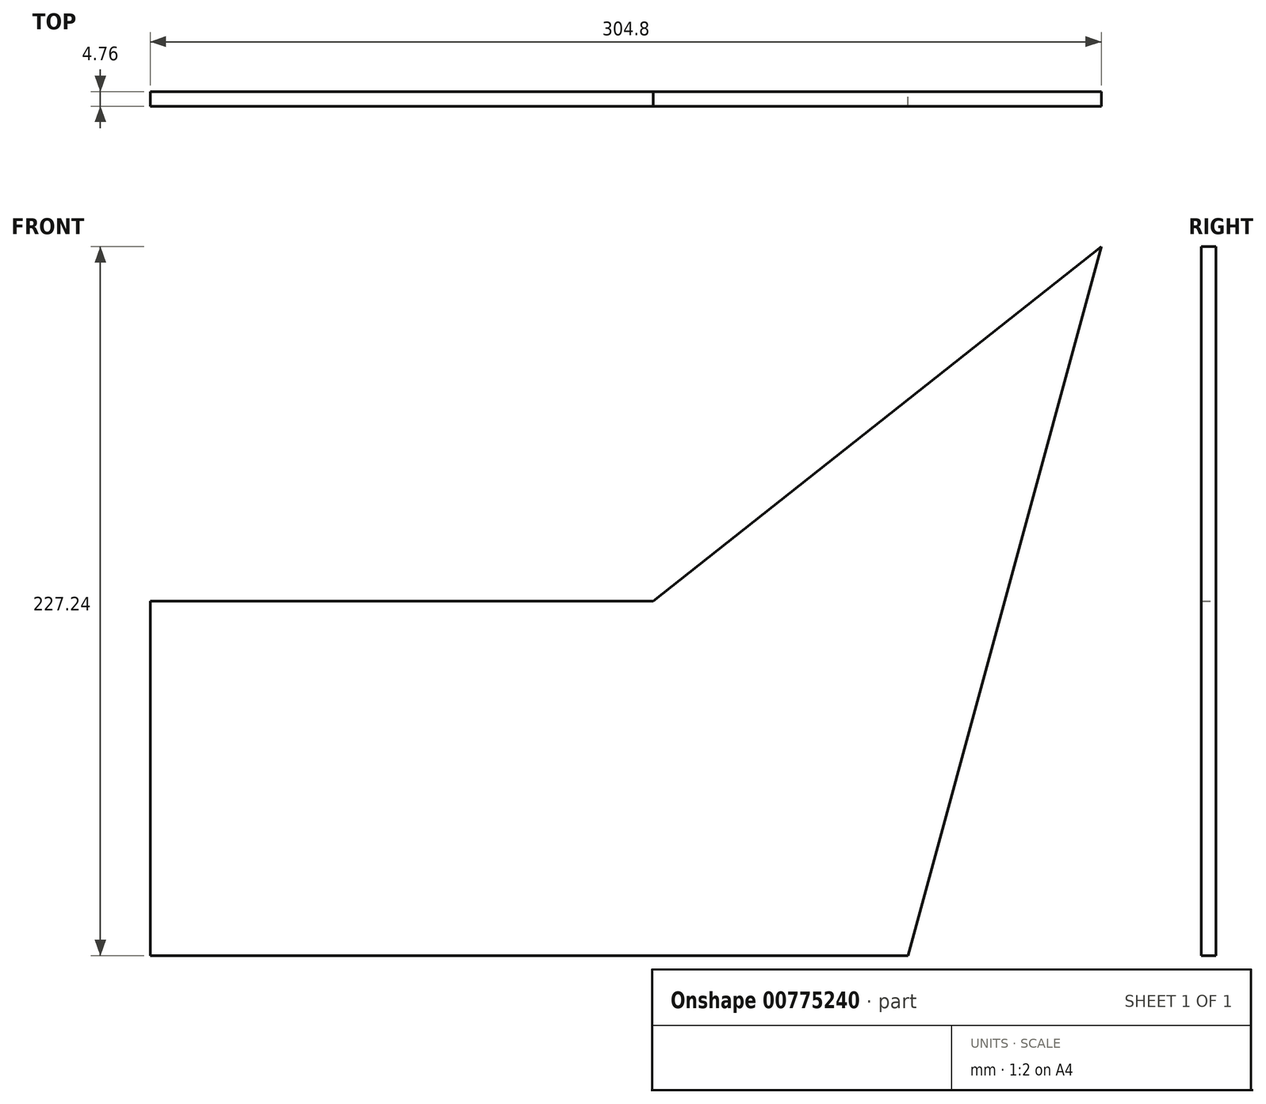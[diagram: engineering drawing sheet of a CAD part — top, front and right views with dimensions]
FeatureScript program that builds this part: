
annotation { "Feature Type Name" : "Feature", "Feature Type Description" : "" }
export const myFeature = defineFeature(function(context is Context, id is Id, definition is map)
    precondition{}
    {
        {
            var Q0;
            Q0=qCreatedBy(makeId("Front.planeOp"),FACE);
            var sketch = newSketch(context, id + "F0", { "sketchPlane" : qUnion([Q0])});
            skLineSegment(sketch, "E0", {"start": v(0, 227.24) * mm, "end": v(-143.66, 113.62) * mm});
            skLineSegment(sketch, "E1", {"start": v(-61.93, 0) * mm, "end": v(-304.8, 0) * mm});
            skLineSegment(sketch, "E2", {"start": v(-304.8, 0) * mm, "end": v(-304.8, 113.62) * mm});
            skLineSegment(sketch, "E3", {"start": v(-304.8, 113.62) * mm, "end": v(-143.66, 113.62) * mm});
            skLineSegment(sketch, "E4", {"start": v(0, 227.24) * mm, "end": v(-61.93, 0) * mm});
            skSolve(sketch);
        }
        {
            var Q0;
            Q0=makeQuery(id+"F0.imprint","IMPRINT",FACE,{"disambiguationData":[TD([[makeQuery(id+"F0.imprint","IMPRINT",EDGE,{"derivedFrom":sQuery(id+"F0.wireOp",EDGE,"tsW24yj8-KVzb-iuXm-R1Pv-bbJQy0zTwmD7")}),1.0]])]});
            var Q1;
            Q1=makeQuery(id+"F0.imprint","IMPRINT",FACE,{"disambiguationData":[TD([[makeQuery(id+"F0.imprint","IMPRINT",EDGE,{"derivedFrom":sQuery(id+"F0.wireOp",EDGE,"E0")}),1.0]])]});
            extrude(context, id + "F1", {"entities" : qUnion([Q0, Q1]), "endBound" : BoundingType.SYMMETRIC, "depth" : 4.76 * mm, "offsetDistance" : 25.4 * mm});
        }
    });
